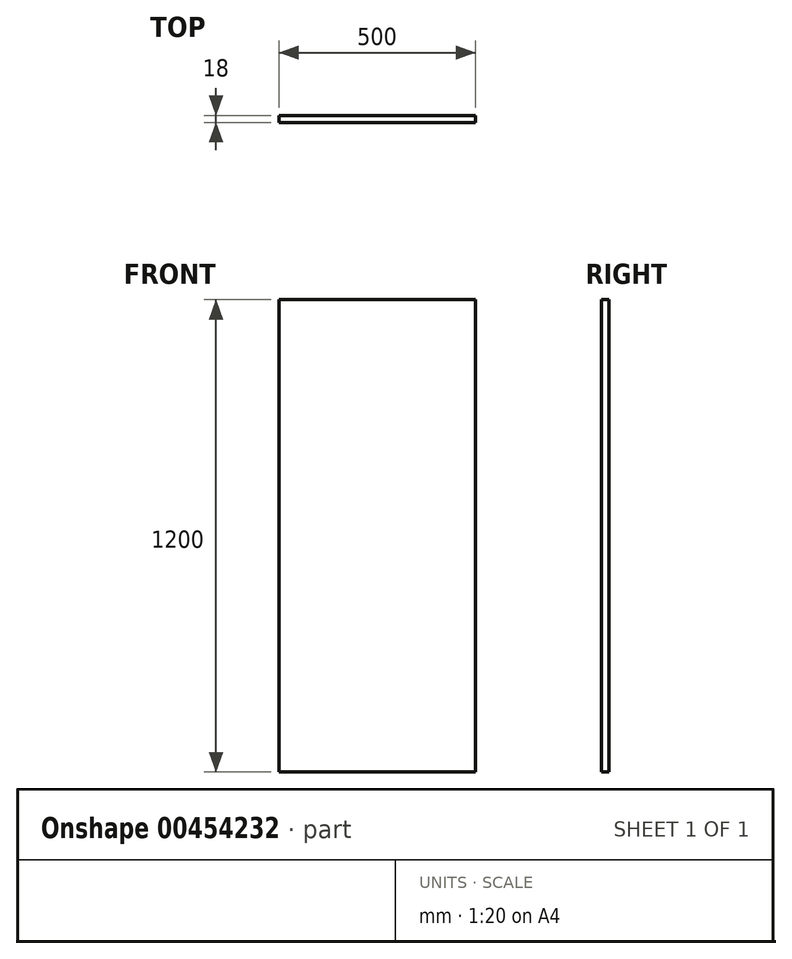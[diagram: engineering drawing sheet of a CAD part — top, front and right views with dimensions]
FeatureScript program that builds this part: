
annotation { "Feature Type Name" : "Feature", "Feature Type Description" : "" }
export const myFeature = defineFeature(function(context is Context, id is Id, definition is map)
    precondition{}
    {
        {
            var Q0;
            Q0=qCreatedBy(makeId("Front.planeOp"),FACE);
            var sketch = newSketch(context, id + "F0", { "sketchPlane" : qUnion([Q0])});
            skLineSegment(sketch, "E0.bottom", {"start": v(-250, -600) * mm, "end": v(250, -600) * mm});
            skLineSegment(sketch, "E0.top", {"start": v(-250, 600) * mm, "end": v(250, 600) * mm});
            skLineSegment(sketch, "E0.left", {"start": v(-250, -600) * mm, "end": v(-250, 600) * mm});
            skLineSegment(sketch, "E0.right", {"start": v(250, -600) * mm, "end": v(250, 600) * mm});
            skPoint(sketch, "E0.middle", {"position": v(0, 0) * mm});
            skSolve(sketch);
        }
        {
            var Q0;
            Q0 = qSketchRegion(id + "F0", true);
            extrude(context, id + "F1", {"entities" : qUnion([Q0]), "depth" : 18 * mm});
        }
    });
